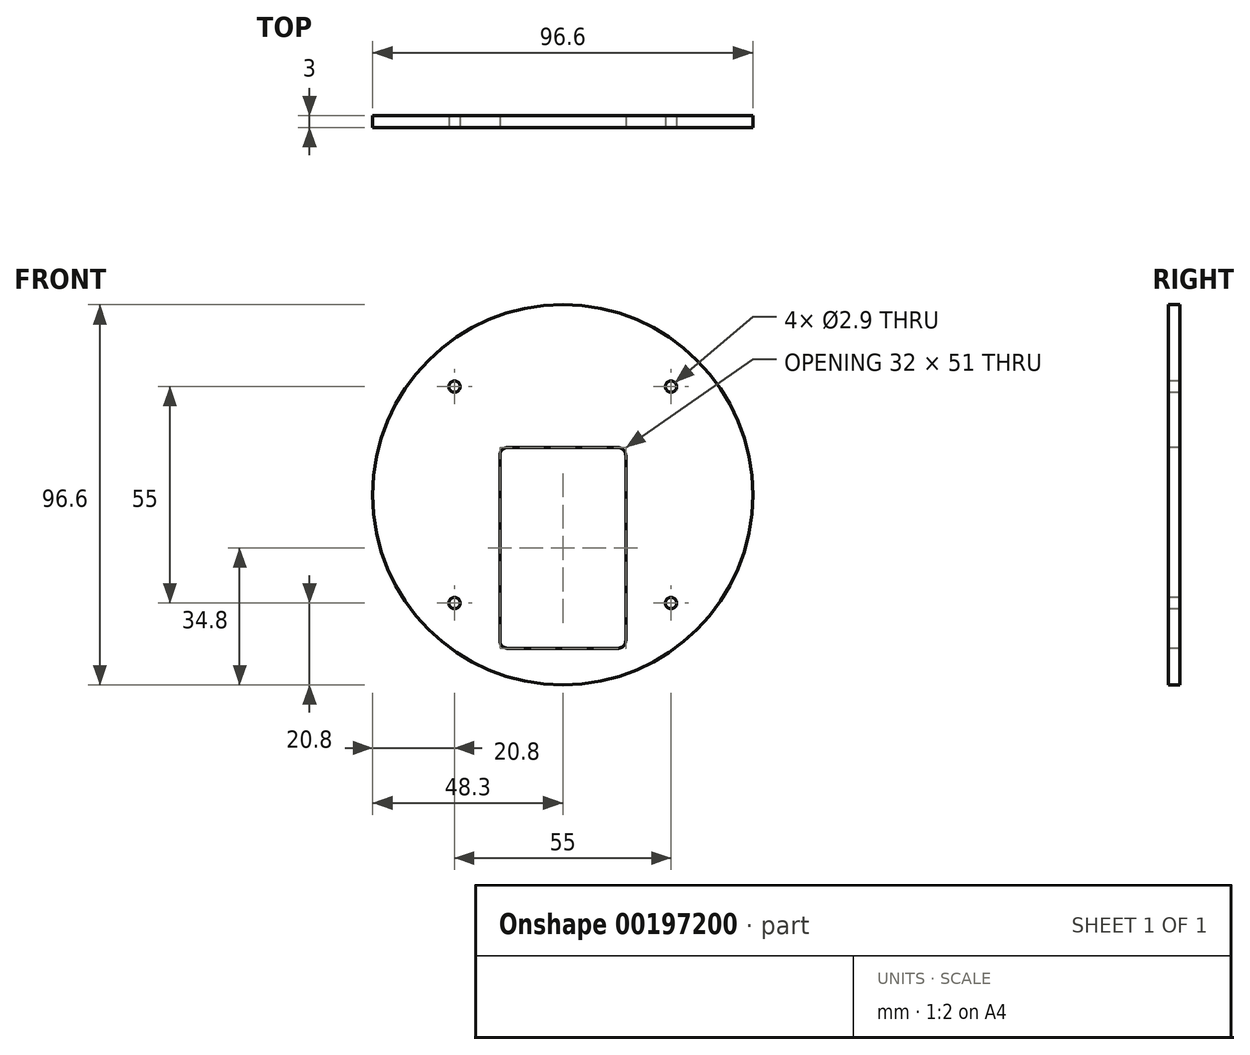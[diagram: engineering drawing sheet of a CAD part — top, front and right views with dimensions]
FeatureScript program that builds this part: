
annotation { "Feature Type Name" : "Feature", "Feature Type Description" : "" }
export const myFeature = defineFeature(function(context is Context, id is Id, definition is map)
    precondition{}
    {
        {
            var Q0;
            Q0=qCreatedBy(makeId("Front.planeOp"),FACE);
            var sketch = newSketch(context, id + "F0", { "sketchPlane" : qUnion([Q0])});
            skCircle(sketch, "E0", {"center": v(0, 0) * mm, "radius": 48.3 * mm});
            skSolve(sketch);
        }
        {
            var Q0;
            Q0=qSketchRegion(id+"F0",true);
            extrude(context, id + "F1", {"entities" : qUnion([Q0]), "depth" : 3 * mm});
        }
        {
            var Q0;
            Q0=makeQuery(id+"F1.opExtrude","CAP_FACE",FACE,{"disambiguationData":[OSD([sQuery(id+"F0.wireOp",EDGE,"E0")])],"isStart":false});
            var sketch = newSketch(context, id + "F2", { "sketchPlane" : qUnion([Q0])});
            skLineSegment(sketch, "E1", {"start": v(-48.3, 0) * mm, "end": v(48.3, 0) * mm, "construction": true});
            skLineSegment(sketch, "E2", {"start": v(0, 0) * mm, "end": v(0, 33.83) * mm, "construction": true});
            skCircle(sketch, "E3", {"center": v(-8, 0) * mm, "radius": 1.25 * mm});
            skCircle(sketch, "E4.MirrorC", {"center": v(8, 0) * mm, "radius": 1.25 * mm});
            skCircle(sketch, "E5", {"center": v(0, 0) * mm, "radius": 2.5 * mm});
            skSolve(sketch);
        }
        {
            var Q0;
            Q0=qSketchRegion(id+"F2",true);
            extrude(context, id + "F3", {"entities" : qUnion([Q0]), "operationType" : NewBodyOperationType.REMOVE, "endBound" : BoundingType.THROUGH_ALL, "oppositeDirection" : true, "depth" : 25 * mm});
        }
        {
            var Q0;
            Q0=makeQuery(id+"F1.opExtrude","CAP_FACE",FACE,{"disambiguationData":[OSD([sQuery(id+"F0.wireOp",EDGE,"E0")])],"isStart":false});
            var sketch = newSketch(context, id + "F4", { "sketchPlane" : qUnion([Q0])});
            skLineSegment(sketch, "E6", {"start": v(0, 0) * mm, "end": v(0, 23.9) * mm, "construction": true});
            skLineSegment(sketch, "E7", {"start": v(0, 0) * mm, "end": v(-31.3, 0) * mm, "construction": true});
            skCircle(sketch, "E8", {"center": v(-27.5, 27.5) * mm, "radius": 1.45 * mm});
            skCircle(sketch, "E9.MirrorC", {"center": v(27.5, 27.5) * mm, "radius": 1.45 * mm});
            skCircle(sketch, "E10.MirrorC", {"center": v(-27.5, -27.5) * mm, "radius": 1.45 * mm});
            skCircle(sketch, "E11.MirrorC", {"center": v(27.5, -27.5) * mm, "radius": 1.45 * mm});
            skSolve(sketch);
        }
        {
            var Q0;
            Q0=qSketchRegion(id+"F4",true);
            extrude(context, id + "F5", {"entities" : qUnion([Q0]), "operationType" : NewBodyOperationType.REMOVE, "endBound" : BoundingType.THROUGH_ALL, "oppositeDirection" : true, "depth" : 25 * mm});
        }
        {
            var Q0;
            Q0=makeQuery(id+"F1.opExtrude","CAP_FACE",FACE,{"disambiguationData":[OSD([sQuery(id+"F0.wireOp",EDGE,"E0")])],"isStart":false});
            var sketch = newSketch(context, id + "F6", { "sketchPlane" : qUnion([Q0])});
            skLineSegment(sketch, "E12", {"start": v(0, 0) * mm, "end": v(0, -47.3) * mm, "construction": true});
            skLineSegment(sketch, "E13.bottom", {"start": v(10.05, -33) * mm, "end": v(-10.05, -33) * mm});
            skLineSegment(sketch, "E13.top", {"start": v(10.05, 0) * mm, "end": v(-10.05, 0) * mm});
            skLineSegment(sketch, "E13.left", {"start": v(10.05, -33) * mm, "end": v(10.05, 0) * mm});
            skLineSegment(sketch, "E13.right", {"start": v(-10.05, -33) * mm, "end": v(-10.05, 0) * mm});
            skPoint(sketch, "E13.middle", {"position": v(0, -16.5) * mm});
            skCircle(sketch, "E14", {"center": v(-13.5, -6.5) * mm, "radius": 1 * mm});
            skLineSegment(sketch, "E15", {"start": v(0, 0) * mm, "end": v(-21.48, 0) * mm, "construction": true});
            skCircle(sketch, "E16.0.1.0", {"center": v(-13.5, -14.5) * mm, "radius": 1 * mm});
            skCircle(sketch, "E16.0.2.0", {"center": v(-13.5, -22.5) * mm, "radius": 1 * mm});
            skCircle(sketch, "E16.0.3.0", {"center": v(-13.5, -30.5) * mm, "radius": 1 * mm});
            skLineSegment(sketch, "E16.direction1", {"start": v(-13.5, -6.5) * mm, "end": v(11.73, -6.5) * mm, "construction": true});
            skLineSegment(sketch, "E16.direction2", {"start": v(-13.5, -6.5) * mm, "end": v(-13.5, -14.5) * mm, "construction": true});
            skCircle(sketch, "E17.MirrorC", {"center": v(13.5, -6.5) * mm, "radius": 1 * mm});
            skCircle(sketch, "E18.MirrorC", {"center": v(13.5, -14.5) * mm, "radius": 1 * mm});
            skCircle(sketch, "E19.MirrorC", {"center": v(13.5, -22.5) * mm, "radius": 1 * mm});
            skCircle(sketch, "E20.MirrorC", {"center": v(13.5, -30.5) * mm, "radius": 1 * mm});
            skCircle(sketch, "E21", {"center": v(0, 0) * mm, "radius": 11.5 * mm});
            skCircle(sketch, "E22", {"center": v(-8, -36) * mm, "radius": 1 * mm});
            skCircle(sketch, "E23.MirrorC", {"center": v(8, -36) * mm, "radius": 1 * mm});
            skSolve(sketch);
        }
        {
            var Q0;
            Q0=qSketchRegion(id+"F6",true);
            extrude(context, id + "F7", {"entities" : qUnion([Q0]), "operationType" : NewBodyOperationType.REMOVE, "endBound" : BoundingType.THROUGH_ALL, "oppositeDirection" : true, "depth" : 25 * mm});
        }
        {
            var Q0;
            Q0=makeQuery(id+"F1.opExtrude","CAP_FACE",FACE,{"disambiguationData":[OSD([sQuery(id+"F0.wireOp",EDGE,"E0")])],"isStart":false});
            var sketch = newSketch(context, id + "F8", { "sketchPlane" : qUnion([Q0])});
            skLineSegment(sketch, "E24", {"start": v(0, 0) * mm, "end": v(0, -53.14) * mm, "construction": true});
            skLineSegment(sketch, "E25.bottom", {"start": v(16, -39) * mm, "end": v(-16, -39) * mm});
            skLineSegment(sketch, "E25.top", {"start": v(16, 12) * mm, "end": v(-16, 12) * mm});
            skLineSegment(sketch, "E25.left", {"start": v(16, -39) * mm, "end": v(16, 12) * mm});
            skLineSegment(sketch, "E25.right", {"start": v(-16, -39) * mm, "end": v(-16, 12) * mm});
            skPoint(sketch, "E25.middle", {"position": v(0, -13.5) * mm});
            skSolve(sketch);
        }
        {
            var Q0;
            Q0 = qSketchRegion(id + "F8", true);
            extrude(context, id + "F9", {"entities" : qUnion([Q0]), "operationType" : NewBodyOperationType.REMOVE, "endBound" : BoundingType.THROUGH_ALL, "oppositeDirection" : true, "depth" : 25 * mm});
        }
        {
            var Q0;
            Q0=makeQuery(id+"F9.boolean.opBoolean","COPY",EDGE,{"derivedFrom":makeQuery(id+"F9.opExtrude","SWEPT_EDGE",EDGE,{"disambiguationData":[OSD([sQuery(id+"F8.wireOp",EDGE,"E25.top"),sQuery(id+"F8.wireOp",EDGE,"E25.right")])]})});
            fillet(context, id + "F10", {"entities" : qUnion([Q0]), "radius" : 2 * mm, "tangentPropagation" : true, "allowEdgeOverflow" : false});
        }
        {
            var Q0;
            Q0=makeQuery(id+"F9.boolean.opBoolean","COPY",EDGE,{"derivedFrom":makeQuery(id+"F9.opExtrude","SWEPT_EDGE",EDGE,{"disambiguationData":[OSD([sQuery(id+"F8.wireOp",EDGE,"E25.top"),sQuery(id+"F8.wireOp",EDGE,"E25.left")])]})});
            fillet(context, id + "F11", {"entities" : qUnion([Q0]), "radius" : 2 * mm, "tangentPropagation" : true, "allowEdgeOverflow" : false});
        }
        {
            var Q0;
            Q0=makeQuery(id+"F9.boolean.opBoolean","COPY",EDGE,{"derivedFrom":makeQuery(id+"F9.opExtrude","SWEPT_EDGE",EDGE,{"disambiguationData":[OSD([sQuery(id+"F8.wireOp",EDGE,"E25.bottom"),sQuery(id+"F8.wireOp",EDGE,"E25.left")])]})});
            var Q1;
            Q1=makeQuery(id+"F9.boolean.opBoolean","COPY",EDGE,{"derivedFrom":makeQuery(id+"F9.opExtrude","SWEPT_EDGE",EDGE,{"disambiguationData":[OSD([sQuery(id+"F8.wireOp",EDGE,"E25.bottom"),sQuery(id+"F8.wireOp",EDGE,"E25.right")])]})});
            fillet(context, id + "F12", {"entities" : qUnion([Q0, Q1]), "radius" : 2 * mm, "tangentPropagation" : true, "allowEdgeOverflow" : false});
        }
    });
